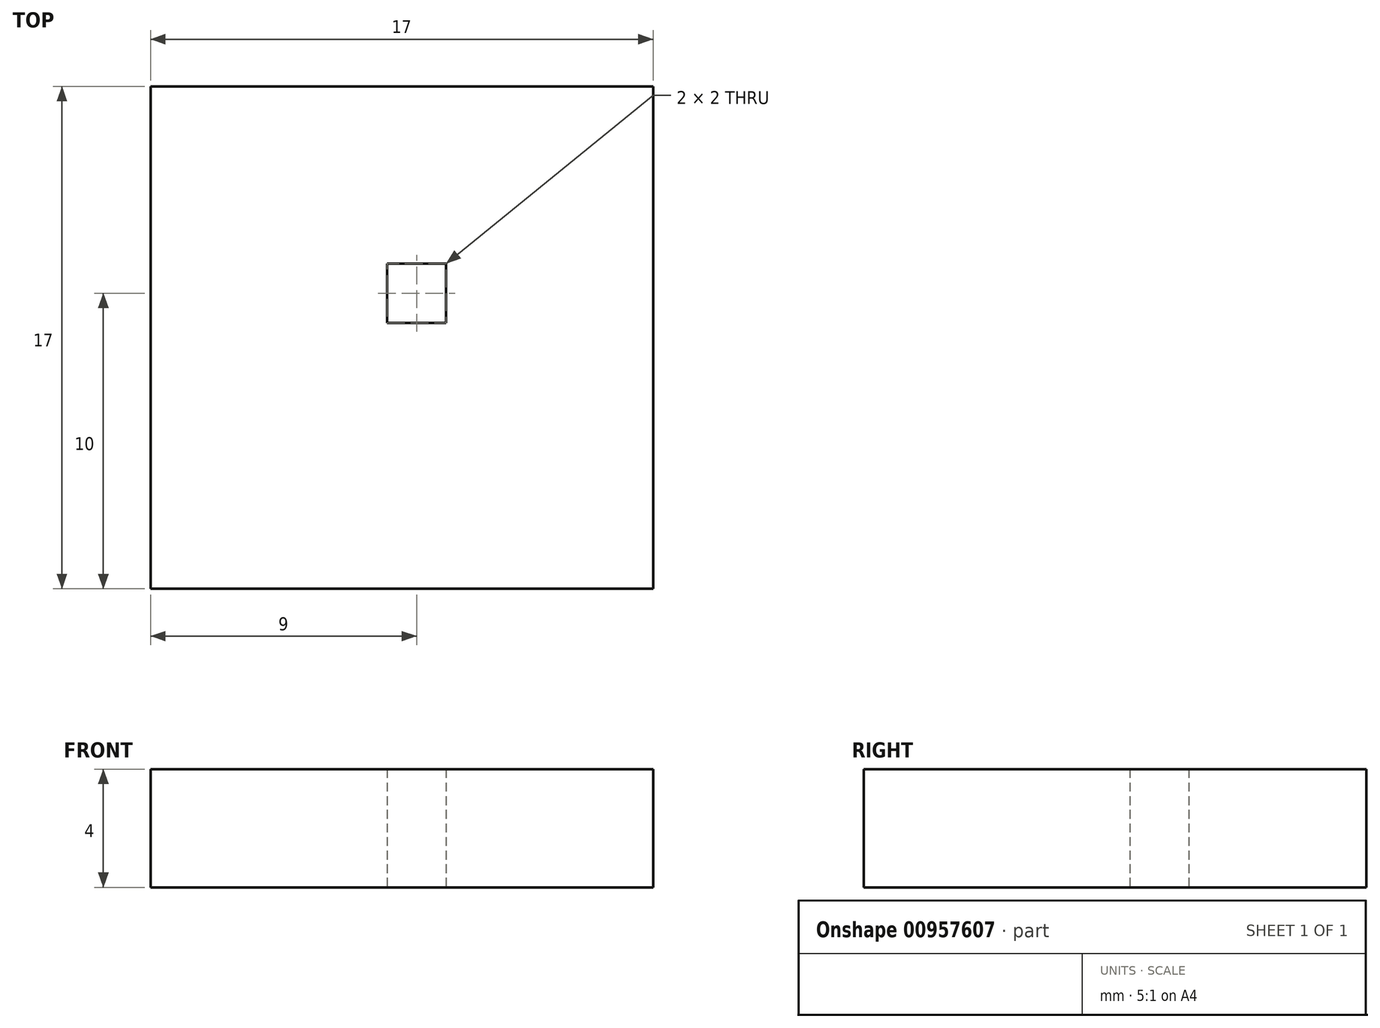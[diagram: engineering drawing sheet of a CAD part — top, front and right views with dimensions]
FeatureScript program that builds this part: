
annotation { "Feature Type Name" : "Feature", "Feature Type Description" : "" }
export const myFeature = defineFeature(function(context is Context, id is Id, definition is map)
    precondition{}
    {
        {
            var Q0;
            Q0=qCreatedBy(makeId("Top.planeOp"),FACE);
            var sketch = newSketch(context, id + "F0", { "sketchPlane" : qUnion([Q0])});
            skLineSegment(sketch, "E0.bottom", {"start": v(-8.5, 8.5) * mm, "end": v(8.5, 8.5) * mm});
            skLineSegment(sketch, "E0.top", {"start": v(-8.5, -8.5) * mm, "end": v(8.5, -8.5) * mm});
            skLineSegment(sketch, "E0.left", {"start": v(-8.5, 8.5) * mm, "end": v(-8.5, -8.5) * mm});
            skLineSegment(sketch, "E0.right", {"start": v(8.5, 8.5) * mm, "end": v(8.5, -8.5) * mm});
            skPoint(sketch, "E0.middle", {"position": v(0, 0) * mm});
            skLineSegment(sketch, "E1.bottom", {"start": v(1.5, 2.5) * mm, "end": v(-0.5, 2.5) * mm});
            skLineSegment(sketch, "E1.top", {"start": v(1.5, 0.5) * mm, "end": v(-0.5, 0.5) * mm});
            skLineSegment(sketch, "E1.left", {"start": v(1.5, 2.5) * mm, "end": v(1.5, 0.5) * mm});
            skLineSegment(sketch, "E1.right", {"start": v(-0.5, 2.5) * mm, "end": v(-0.5, 0.5) * mm});
            skSolve(sketch);
        }
        {
            var Q0;
            Q0=makeQuery(id+"F0.imprint","IMPRINT",FACE,{"disambiguationData":[TD([[makeQuery(id+"F0.imprint","IMPRINT",EDGE,{"derivedFrom":sQuery(id+"F0.wireOp",EDGE,"E0.bottom")}),-1.0]])]});
            extrude(context, id + "F1", {"entities" : qUnion([Q0]), "depth" : 4 * mm, "offsetDistance" : 25 * mm});
        }
    });
